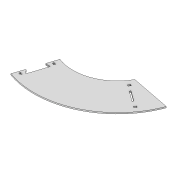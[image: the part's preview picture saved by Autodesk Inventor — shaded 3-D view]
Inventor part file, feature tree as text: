
AUTODESK INVENTOR PART (.ipt)
format: ipt  version: 2020 (Build 240168000, 168)  size: 270,848 bytes
history: native  units: mm
features: extrude x1, sketch x1
ambient origin geometry x8: Origin, YZ Plane, XZ Plane, XY Plane, X Axis, Y Axis, Z Axis, Center Point
bodies: Solid1 (feature_tree)
feature tree (2):
  extrude  "Extrusion1"  Depth=1.75mm
  sketch  "Sketch1"  dims[d0=504.787567mm d1=944.787567mm d2=50.0mm d4=360.0deg d6=7.5mm d7=7.5mm d9=68.5mm d10=7.5mm d11=7.5mm d12=3.5mm d13=3.5mm d17=50.0mm d19=360.0deg d21=4.363323mm d25=10.0mm d26=10.0mm d27=1.75mm d28=30.0mm d30=25.132741mm d32=7.0mm d33=0.0mm d34=0.0mm d35=8.0mm d36=1.75mm d38=50.0mm d40=50.0mm d42=30.0mm d43=8.0mm d44=1.75mm d45=50.0mm d47=360.0deg]
